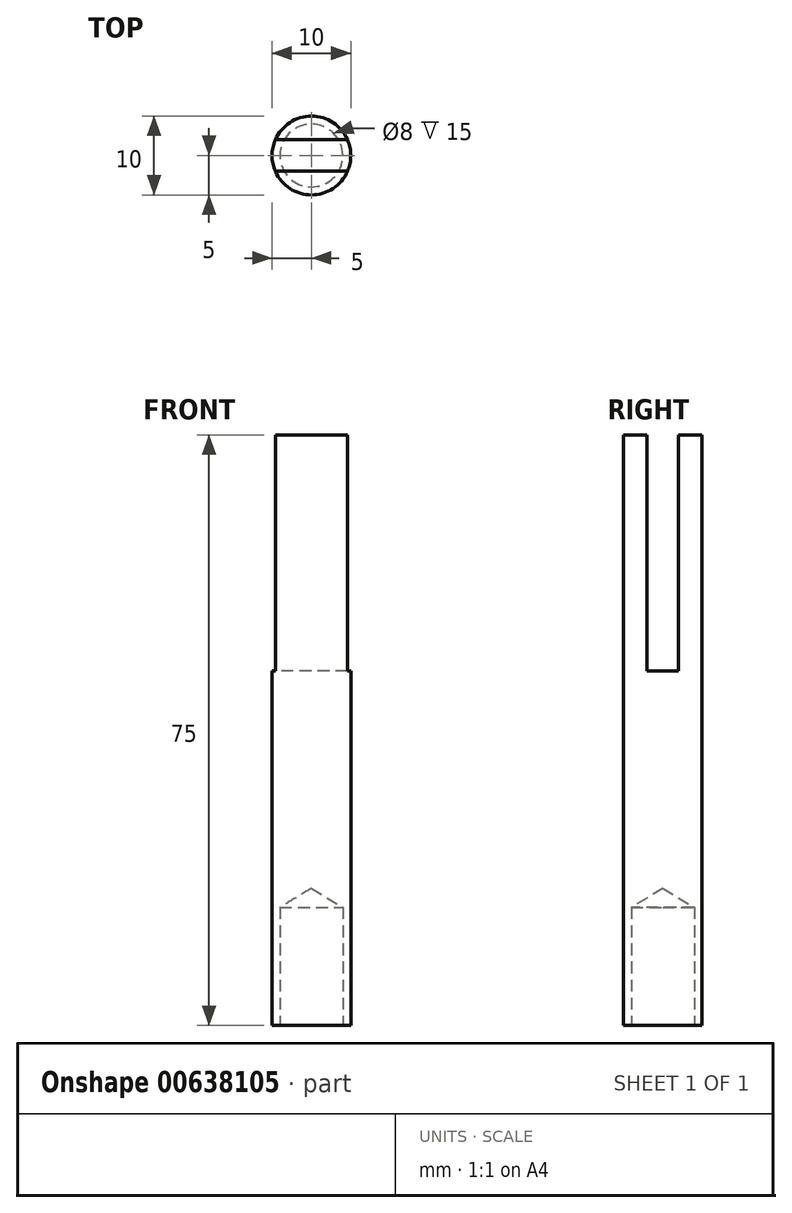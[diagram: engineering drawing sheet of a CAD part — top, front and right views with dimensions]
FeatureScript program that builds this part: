
annotation { "Feature Type Name" : "Feature", "Feature Type Description" : "" }
export const myFeature = defineFeature(function(context is Context, id is Id, definition is map)
    precondition{}
    {
        {
            var Q0;
            Q0=qCreatedBy(makeId("Top.planeOp"),FACE);
            var sketch = newSketch(context, id + "F0", { "sketchPlane" : qUnion([Q0])});
            skCircle(sketch, "E0", {"center": v(0, 0) * mm, "radius": 5 * mm});
            skSolve(sketch);
        }
        {
            var Q0;
            Q0 = qSketchRegion(id + "F0", true);
            extrude(context, id + "F1", {"entities" : qUnion([Q0]), "depth" : 75 * mm, "offsetDistance" : 25 * mm});
        }
        {
            var Q0;
            Q0=makeQuery(id+"F1.opExtrude","CAP_FACE",FACE,{"disambiguationData":[OSD([sQuery(id+"F0.wireOp",EDGE,"E0")])],"isStart":true});
            var sketch = newSketch(context, id + "F2", { "sketchPlane" : qUnion([Q0])});
            skCircle(sketch, "E1", {"center": v(0, 0) * mm, "radius": 4 * mm});
            skSolve(sketch);
        }
        {
            var Q0;
            Q0=sQuery(id+"F2.wireOp",VERTEX,"E1.center");
            var Q1;
            Q1=makeQuery(id+"F1.opExtrude","SWEPT_BODY",BODY,{"disambiguationData":[OSD([sQuery(id+"F0.wireOp",EDGE,"E0")])]});
            hole(context, id + "F3", {"style" : HoleStyle.SIMPLE, "endStyle" : HoleEndStyle.BLIND, "holeDiameter" : 8 * mm, "majorDiameter" : 5 * mm, "holeDepth" : 15 * mm, "isTappedThrough" : true, "tappedDepth" : 12 * mm, "tapClearance" : 3, "locations" : qUnion([Q0]), "scope" : qUnion([Q1])});
        }
        {
            var Q0;
            Q0=qCreatedBy(makeId("Right.planeOp"),FACE);
            var sketch = newSketch(context, id + "F4", { "sketchPlane" : qUnion([Q0])});
            skLineSegment(sketch, "E2.bottom", {"start": v(-2, 75) * mm, "end": v(2, 75) * mm});
            skLineSegment(sketch, "E2.top", {"start": v(-2, 45) * mm, "end": v(2, 45) * mm});
            skLineSegment(sketch, "E2.left", {"start": v(-2, 75) * mm, "end": v(-2, 45) * mm});
            skLineSegment(sketch, "E2.right", {"start": v(2, 75) * mm, "end": v(2, 45) * mm});
            skLineSegment(sketch, "E3", {"start": v(0, 75) * mm, "end": v(0, 45) * mm});
            skSolve(sketch);
        }
        {
            var Q0;
            Q0 = qSketchRegion(id + "F4", true);
            extrude(context, id + "F5", {"entities" : qUnion([Q0]), "operationType" : NewBodyOperationType.REMOVE, "endBound" : BoundingType.SYMMETRIC, "depth" : 25 * mm, "offsetDistance" : 25 * mm});
        }
    });
